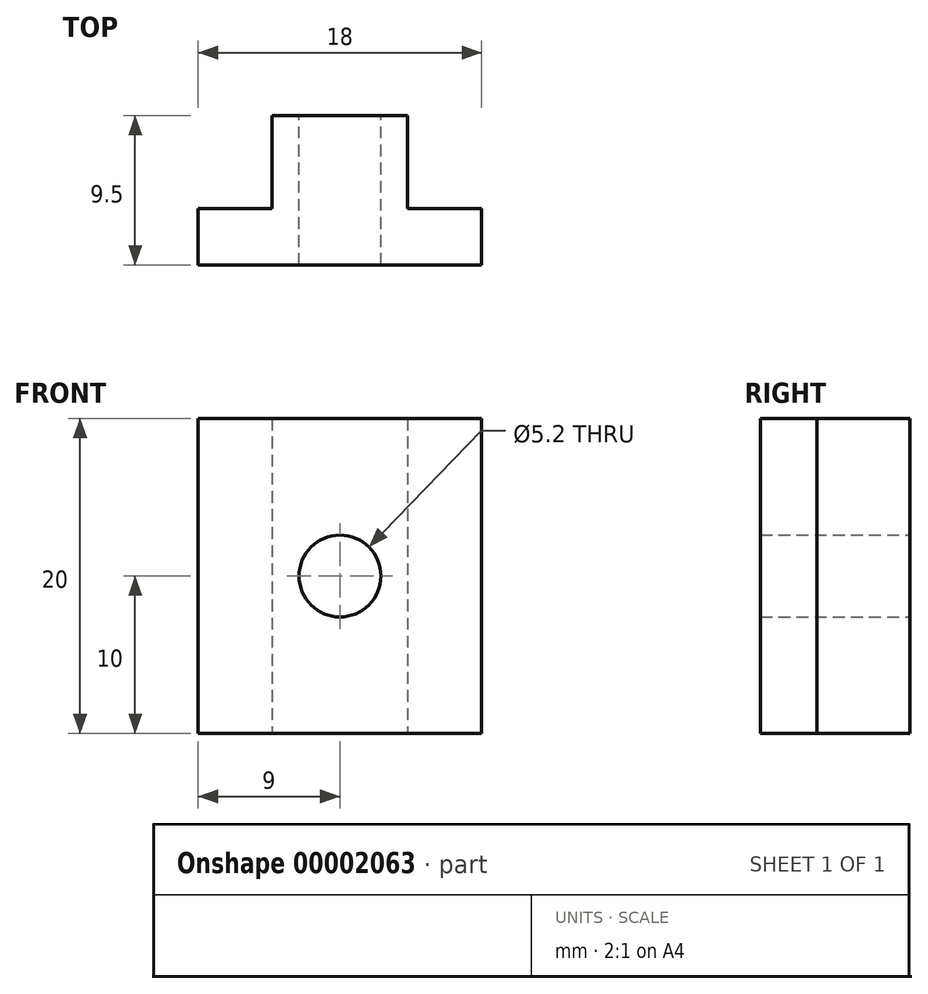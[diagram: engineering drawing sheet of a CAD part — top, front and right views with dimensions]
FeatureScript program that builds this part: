
annotation { "Feature Type Name" : "Feature", "Feature Type Description" : "" }
export const myFeature = defineFeature(function(context is Context, id is Id, definition is map)
    precondition{}
    {
        {
            var Q0;
            Q0=qCreatedBy(makeId("Top.planeOp"),FACE);
            var sketch = newSketch(context, id + "F0", { "sketchPlane" : qUnion([Q0])});
            skLineSegment(sketch, "E0.rect.bottom", {"start": v(9, -4.75) * mm, "end": v(-9, -4.75) * mm});
            skLineSegment(sketch, "E0.rect.top", {"start": v(9, 4.75) * mm, "end": v(-9, 4.75) * mm});
            skLineSegment(sketch, "E0.rect.left", {"start": v(9, -4.75) * mm, "end": v(9, 4.75) * mm});
            skLineSegment(sketch, "E0.rect.right", {"start": v(-9, -4.75) * mm, "end": v(-9, 4.75) * mm});
            skPoint(sketch, "E0.rect.middle", {"position": v(0, 0) * mm});
            skLineSegment(sketch, "E1.bottom", {"start": v(-9, 4.75) * mm, "end": v(-4.3, 4.75) * mm});
            skLineSegment(sketch, "E1.top", {"start": v(-9, -1.15) * mm, "end": v(-4.3, -1.15) * mm});
            skLineSegment(sketch, "E1.left", {"start": v(-9, 4.75) * mm, "end": v(-9, -1.15) * mm});
            skLineSegment(sketch, "E1.right", {"start": v(-4.3, 4.75) * mm, "end": v(-4.3, -1.15) * mm});
            skLineSegment(sketch, "E2.0.MirrorCS", {"start": v(4.3, 4.75) * mm, "end": v(4.3, -1.15) * mm});
            skLineSegment(sketch, "E3.0.MirrorCS", {"start": v(9, -1.15) * mm, "end": v(4.3, -1.15) * mm});
            skLineSegment(sketch, "E4.0.MirrorCS", {"start": v(9, 4.75) * mm, "end": v(9, -1.15) * mm});
            skLineSegment(sketch, "E5.0.MirrorCS", {"start": v(9, 4.75) * mm, "end": v(4.3, 4.75) * mm});
            skSolve(sketch);
        }
        {
            var Q0;
            Q0=makeQuery(id+"F0.imprint","IMPRINT",FACE,{"disambiguationData":[TD([[makeQuery(id+"F0.imprint","IMPRINT",EDGE,{"derivedFrom":sQuery(id+"F0.wireOp",EDGE,"E0.rect.bottom")}),-1.0]])]});
            extrude(context, id + "F1", {"entities" : qUnion([Q0]), "endBound" : BoundingType.SYMMETRIC, "depth" : 20 * mm});
        }
        {
            var Q0;
            Q0=makeQuery(id+"F1.opExtrude","SWEPT_FACE",FACE,{"disambiguationData":[OSD([sQuery(id+"F0.wireOp",EDGE,"E0.rect.top")])]});
            var sketch = newSketch(context, id + "F2", { "sketchPlane" : qUnion([Q0])});
            skCircle(sketch, "E6", {"center": v(0, 0) * mm, "radius": 2.6 * mm});
            skSolve(sketch);
        }
        {
            var Q0;
            Q0=makeQuery(id+"F2.imprint","IMPRINT",FACE,{"disambiguationData":[TD([[makeQuery(id+"F2.imprint","IMPRINT",EDGE,{"derivedFrom":sQuery(id+"F2.wireOp",EDGE,"E6")}),1.0]])]});
            extrude(context, id + "F3", {"entities" : qUnion([Q0]), "operationType" : NewBodyOperationType.REMOVE, "endBound" : BoundingType.THROUGH_ALL, "oppositeDirection" : true, "depth" : 25 * mm});
        }
    });
